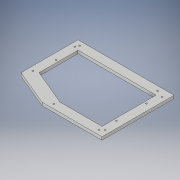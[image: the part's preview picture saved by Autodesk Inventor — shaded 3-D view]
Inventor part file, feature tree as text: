
AUTODESK INVENTOR PART (.ipt)
format: ipt  version: 2018 (Build 220112000, 112)  size: 165,376 bytes
history: native  units: in
note: dims shown in document units (in); Inventor stores cm internally (conversion verified against a paired STEP export)
features: extrude x3, sketch x3, projected_geometry x1
ambient origin geometry x8: Origin, YZ Plane, XZ Plane, XY Plane, X Axis, Y Axis, Z Axis, Center Point
bodies: Solid1 (feature_tree)
feature tree (7):
  extrude  "Extrusion1"  Depth=8.0in
  extrude  "Extrusion2"  Depth=6.0in
  extrude  "Extrusion3"  Depth=0.25in
  sketch  "Sketch1"  dims[d0=4.75in d1=8.0in]
  sketch  "Sketch3"  dims[d2=5.0in d3=6.0in]
  projected_geometry  "Projected Loop1"
  sketch  "Sketch4"  dims[d4=0.25in d5=0.0in d10=4.75in d11=3.25in d12=8.0in d13=6.5in d14=4.5in d15=3.5in d16=0.75in d17=0.75in d18=0.12in d19=0.12in d20=4.75in d21=0.12in d22=0.12in d23=0.625in d24=0.365in d25=0.365in d26=0.365in d27=1.0in d28=0.5in d29=0.365in d30=0.12in d31=0.12in d32=3.5in d33=0.625in d34=0.365in d35=0.365in d36=0.12in d37=0.365in d38=0.625in d39=0.12in d40=0.625in d41=0.365in d42=0.25in d43=0.0in d44=0.12in d45=0.12in d46=0.12in d47=3.25in d48=1.625in d49=0.2in d50=1.0in d51=1.0in d52=0.2in d53=0.2in d54=0.25in d55=0.0in]
